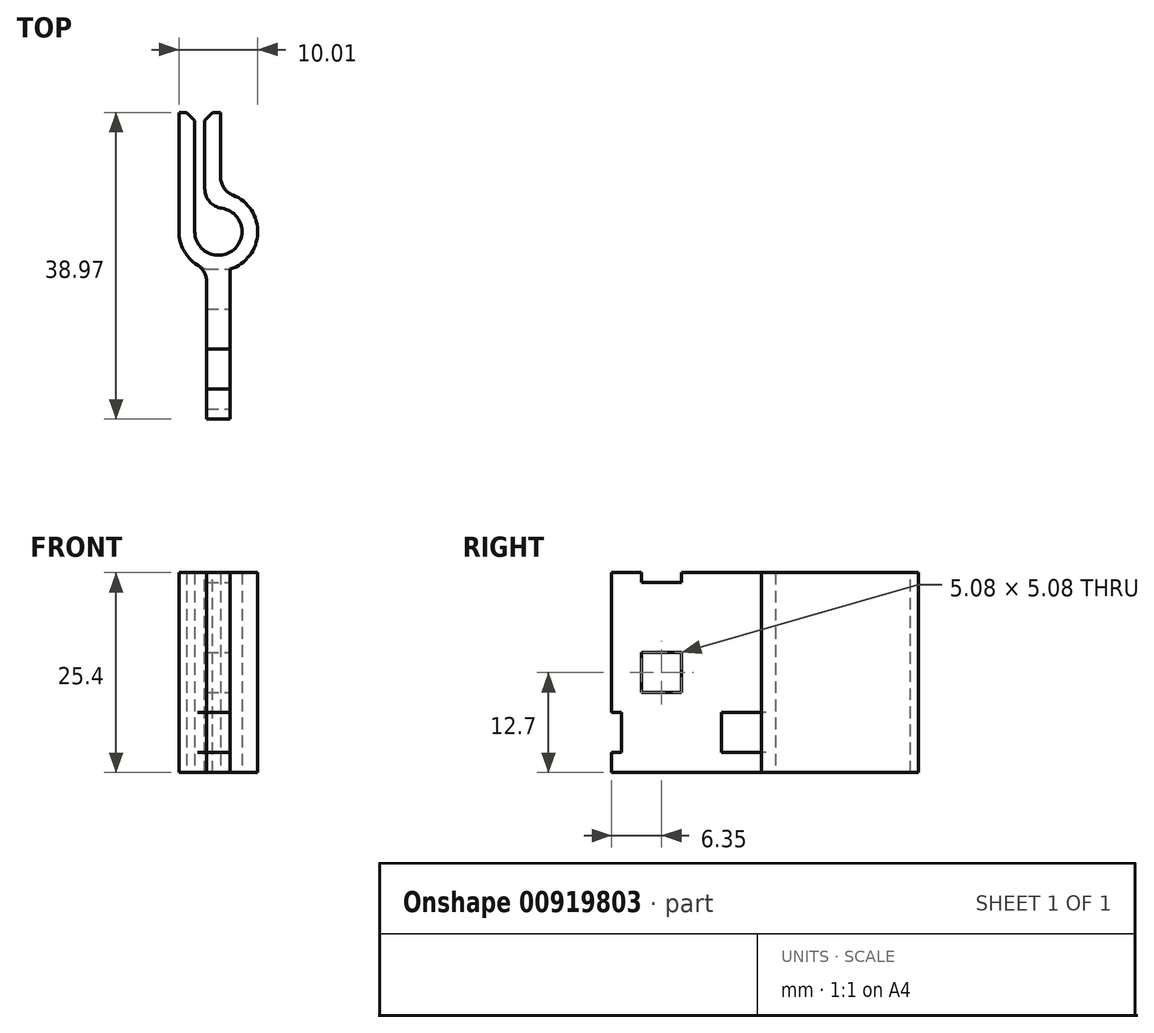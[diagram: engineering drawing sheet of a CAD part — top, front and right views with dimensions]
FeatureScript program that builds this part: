
annotation { "Feature Type Name" : "Feature", "Feature Type Description" : "" }
export const myFeature = defineFeature(function(context is Context, id is Id, definition is map)
    precondition{}
    {
        {
            var Q0;
            Q0=qCreatedBy(makeId("Top.planeOp"),FACE);
            var sketch = newSketch(context, id + "F0", { "sketchPlane" : qUnion([Q0])});
            skArc(sketch, "E0", {"start": v(0.64, 2.45) * mm, "mid": v(5.03, -1.38) * mm, "end": v(-0.64, 0) * mm});
            skLineSegment(sketch, "E1", {"start": v(-0.64, 0) * mm, "end": v(-0.64, 15.15) * mm});
            skLineSegment(sketch, "E2", {"start": v(0.64, 15.15) * mm, "end": v(0.64, 2.45) * mm});
            skLineSegment(sketch, "E3.0", {"start": v(-2.64, 0) * mm, "end": v(-2.64, 15.15) * mm});
            skArc(sketch, "E3.1", {"start": v(2.64, 5) * mm, "mid": v(5.8, -3.63) * mm, "end": v(-2.64, 0) * mm});
            skLineSegment(sketch, "E3.2", {"start": v(2.64, 15.15) * mm, "end": v(2.64, 5) * mm});
            skLineSegment(sketch, "E4", {"start": v(-2.63, 15.15) * mm, "end": v(-0.63, 15.15) * mm});
            skLineSegment(sketch, "E5", {"start": v(0.63, 15.15) * mm, "end": v(2.63, 15.15) * mm});
            skLineSegment(sketch, "E6", {"start": v(-0.64, 6.55) * mm, "end": v(0.64, 6.55) * mm, "construction": true});
            skPoint(sketch, "E7", {"position": v(0, 6.55) * mm});
            skSolve(sketch);
        }
        {
            var Q0;
            Q0 = qSketchRegion(id + "F0", true);
            extrude(context, id + "F1", {"entities" : qUnion([Q0]), "depth" : 25.4 * mm, "offsetDistance" : 25.4 * mm});
        }
        {
            var Q0;
            Q0=makeQuery(id+"F1.opExtrude","SWEPT_EDGE",EDGE,{"disambiguationData":[OSD([sQuery(id+"F0.wireOp",EDGE,"E1"),sQuery(id+"F0.wireOp",EDGE,"E4")])]});
            var Q1;
            Q1=makeQuery(id+"F1.opExtrude","SWEPT_EDGE",EDGE,{"disambiguationData":[OSD([sQuery(id+"F0.wireOp",EDGE,"E2"),sQuery(id+"F0.wireOp",EDGE,"E5")])]});
            chamfer(context, id + "F2", {"entities" : qUnion([Q0, Q1]), "width" : 1.02 * mm, "tangentPropagation" : true});
        }
        {
            var Q0;
            Q0=qCreatedBy(makeId("Top.planeOp"),FACE);
            var sketch = newSketch(context, id + "F3", { "sketchPlane" : qUnion([Q0])});
            skLineSegment(sketch, "E8.bottom", {"start": v(0.86, -4.77) * mm, "end": v(3.86, -4.77) * mm});
            skLineSegment(sketch, "E8.top", {"start": v(0.86, -23.82) * mm, "end": v(3.86, -23.82) * mm});
            skLineSegment(sketch, "E8.left", {"start": v(0.86, -4.77) * mm, "end": v(0.86, -23.82) * mm});
            skLineSegment(sketch, "E8.right", {"start": v(3.86, -4.77) * mm, "end": v(3.86, -23.82) * mm});
            skPoint(sketch, "E9", {"position": v(2.36, -4.77) * mm});
            skPoint(sketch, "E10", {"position": v(2.36, 0) * mm});
            skSolve(sketch);
        }
        {
            var Q0;
            Q0 = qSketchRegion(id + "F3", true);
            var Q1;
            Q1=makeQuery(id+"F1.opExtrude","CAP_FACE",FACE,{"disambiguationData":[OSD([sQuery(id+"F0.wireOp",EDGE,"E0"),sQuery(id+"F0.wireOp",EDGE,"E1"),sQuery(id+"F0.wireOp",EDGE,"E2"),sQuery(id+"F0.wireOp",EDGE,"E3.0"),sQuery(id+"F0.wireOp",EDGE,"E3.1"),sQuery(id+"F0.wireOp",EDGE,"E3.2"),sQuery(id+"F0.wireOp",EDGE,"E4"),sQuery(id+"F0.wireOp",EDGE,"E5")])],"isStart":false});
            extrude(context, id + "F4", {"entities" : qUnion([Q0]), "operationType" : NewBodyOperationType.ADD, "endBound" : BoundingType.UP_TO_SURFACE, "depth" : 25.4 * mm, "endBoundEntityFace" : qUnion([Q1]), "offsetDistance" : 25.4 * mm});
        }
        {
            var Q0;
            Q0=makeQuery(id+"F4.opExtrude","SWEPT_FACE",FACE,{"disambiguationData":[OSD([sQuery(id+"F3.wireOp",EDGE,"E8.right")])]});
            var sketch = newSketch(context, id + "F5", { "sketchPlane" : qUnion([Q0])});
            skLineSegment(sketch, "E11.bottom", {"start": v(-4.77, 2.54) * mm, "end": v(-9.85, 2.54) * mm});
            skLineSegment(sketch, "E11.top", {"start": v(-4.77, 7.62) * mm, "end": v(-9.85, 7.62) * mm});
            skLineSegment(sketch, "E11.left", {"start": v(-4.77, 2.54) * mm, "end": v(-4.77, 7.62) * mm});
            skLineSegment(sketch, "E11.right", {"start": v(-9.85, 2.54) * mm, "end": v(-9.85, 7.62) * mm});
            skLineSegment(sketch, "E12.bottom", {"start": v(-20, 10.16) * mm, "end": v(-14.93, 10.16) * mm});
            skLineSegment(sketch, "E12.top", {"start": v(-20, 15.24) * mm, "end": v(-14.93, 15.24) * mm});
            skLineSegment(sketch, "E12.left", {"start": v(-20, 10.16) * mm, "end": v(-20, 15.24) * mm});
            skLineSegment(sketch, "E12.right", {"start": v(-14.93, 10.16) * mm, "end": v(-14.93, 15.24) * mm});
            skLineSegment(sketch, "E13.bottom", {"start": v(-23.82, 2.54) * mm, "end": v(-22.55, 2.54) * mm});
            skLineSegment(sketch, "E13.top", {"start": v(-23.82, 7.62) * mm, "end": v(-22.55, 7.62) * mm});
            skLineSegment(sketch, "E13.left", {"start": v(-23.82, 2.54) * mm, "end": v(-23.82, 7.62) * mm});
            skLineSegment(sketch, "E13.right", {"start": v(-22.55, 2.54) * mm, "end": v(-22.55, 7.62) * mm});
            skLineSegment(sketch, "E14.bottom", {"start": v(-20, 25.4) * mm, "end": v(-14.93, 25.4) * mm});
            skLineSegment(sketch, "E14.top", {"start": v(-20, 24.13) * mm, "end": v(-14.93, 24.13) * mm});
            skLineSegment(sketch, "E14.left", {"start": v(-20, 25.4) * mm, "end": v(-20, 24.13) * mm});
            skLineSegment(sketch, "E14.right", {"start": v(-14.93, 25.4) * mm, "end": v(-14.93, 24.13) * mm});
            skSolve(sketch);
        }
        {
            var Q0;
            Q0 = qSketchRegion(id + "F5", true);
            extrude(context, id + "F6", {"entities" : qUnion([Q0]), "operationType" : NewBodyOperationType.REMOVE, "endBound" : BoundingType.THROUGH_ALL, "oppositeDirection" : true, "depth" : 25.4 * mm, "offsetDistance" : 25.4 * mm});
        }
        {
            var Q0;
            Q0=makeQuery(id+"F1.opExtrude","SWEPT_EDGE",EDGE,{"disambiguationData":[OSD([sQuery(id+"F0.wireOp",EDGE,"E0"),sQuery(id+"F0.wireOp",EDGE,"E2")])]});
            var Q1;
            Q1=makeQuery(id+"F1.opExtrude","SWEPT_EDGE",EDGE,{"disambiguationData":[OSD([sQuery(id+"F0.wireOp",EDGE,"E3.0"),sQuery(id+"F0.wireOp",EDGE,"E3.1")])]});
            var Q2;
            Q2=makeQuery(id+"F1.opExtrude","SWEPT_EDGE",EDGE,{"disambiguationData":[OSD([sQuery(id+"F0.wireOp",EDGE,"E3.1"),sQuery(id+"F0.wireOp",EDGE,"E3.2")])]});
            var Q3;
            {var subQ0=sQuery(id+"F3.wireOp",EDGE,"E8.right");var subQ1=sQuery(id+"F3.wireOp",EDGE,"E8.bottom");Q3=makeQuery(id+"F6.boolean.opBoolean","SPLIT",EDGE,{"disambiguationData":[TD([makeQuery(id+"F6.opExtrude","SWEPT_FACE",FACE,{"disambiguationData":[OSD([sQuery(id+"F5.wireOp",EDGE,"E11.top")])]})])],"derivedFrom":makeQuery(id+"F4.opExtrude","SWEPT_EDGE",EDGE,{"disambiguationData":[OSD([subQ1,subQ0])]})});}
            var Q4;
            {var subQ0=sQuery(id+"F3.wireOp",EDGE,"E8.right");var subQ1=sQuery(id+"F3.wireOp",EDGE,"E8.bottom");Q4=makeQuery(id+"F6.boolean.opBoolean","SPLIT",EDGE,{"disambiguationData":[TD([makeQuery(id+"F6.opExtrude","SWEPT_FACE",FACE,{"disambiguationData":[OSD([sQuery(id+"F5.wireOp",EDGE,"E11.bottom")])]})])],"derivedFrom":makeQuery(id+"F4.opExtrude","SWEPT_EDGE",EDGE,{"disambiguationData":[OSD([subQ1,subQ0])]})});}
            var Q5;
            {var subQ0=sQuery(id+"F3.wireOp",EDGE,"E8.left");var subQ1=makeQuery(id+"F4.opExtrude","SWEPT_FACE",FACE,{"disambiguationData":[OSD([subQ0])]});var subQ2=sQuery(id+"F3.wireOp",EDGE,"E8.bottom");var subQ3=sQuery(id+"F0.wireOp",EDGE,"E3.1");var subQ4=makeQuery(id+"F1.opExtrude","SWEPT_FACE",FACE,{"disambiguationData":[OSD([subQ3])]});Q5=makeQuery(id+"F6.boolean.opBoolean","SPLIT",EDGE,{"disambiguationData":[topologyDisambiguationEdgeConnected([subQ4,subQ1]),TD([makeQuery(id+"F6.opExtrude","SWEPT_FACE",FACE,{"disambiguationData":[OSD([sQuery(id+"F5.wireOp",EDGE,"E11.top")])]})])],"derivedFrom":makeQuery(id+"F4.opExtrude","SWEPT_EDGE",EDGE,{"disambiguationData":[OSD([subQ2,subQ0])]})});}
            var Q6;
            {var subQ0=sQuery(id+"F3.wireOp",EDGE,"E8.left");var subQ1=makeQuery(id+"F4.opExtrude","SWEPT_FACE",FACE,{"disambiguationData":[OSD([subQ0])]});var subQ2=sQuery(id+"F3.wireOp",EDGE,"E8.bottom");var subQ3=sQuery(id+"F0.wireOp",EDGE,"E3.1");var subQ4=makeQuery(id+"F1.opExtrude","SWEPT_FACE",FACE,{"disambiguationData":[OSD([subQ3])]});Q6=makeQuery(id+"F6.boolean.opBoolean","SPLIT",EDGE,{"disambiguationData":[topologyDisambiguationEdgeConnected([subQ4,subQ1]),TD([makeQuery(id+"F6.opExtrude","SWEPT_FACE",FACE,{"disambiguationData":[OSD([sQuery(id+"F5.wireOp",EDGE,"E11.bottom")])]})])],"derivedFrom":makeQuery(id+"F4.opExtrude","SWEPT_EDGE",EDGE,{"disambiguationData":[OSD([subQ2,subQ0])]})});}
            fillet(context, id + "F7", {"entities" : qUnion([Q0, Q1, Q2, Q3, Q4, Q5, Q6]), "radius" : 2.5 * mm, "tangentPropagation" : true, "defaultsChanged" : false, "vertexSettings" : [], "allowEdgeOverflow" : false});
        }
    });
